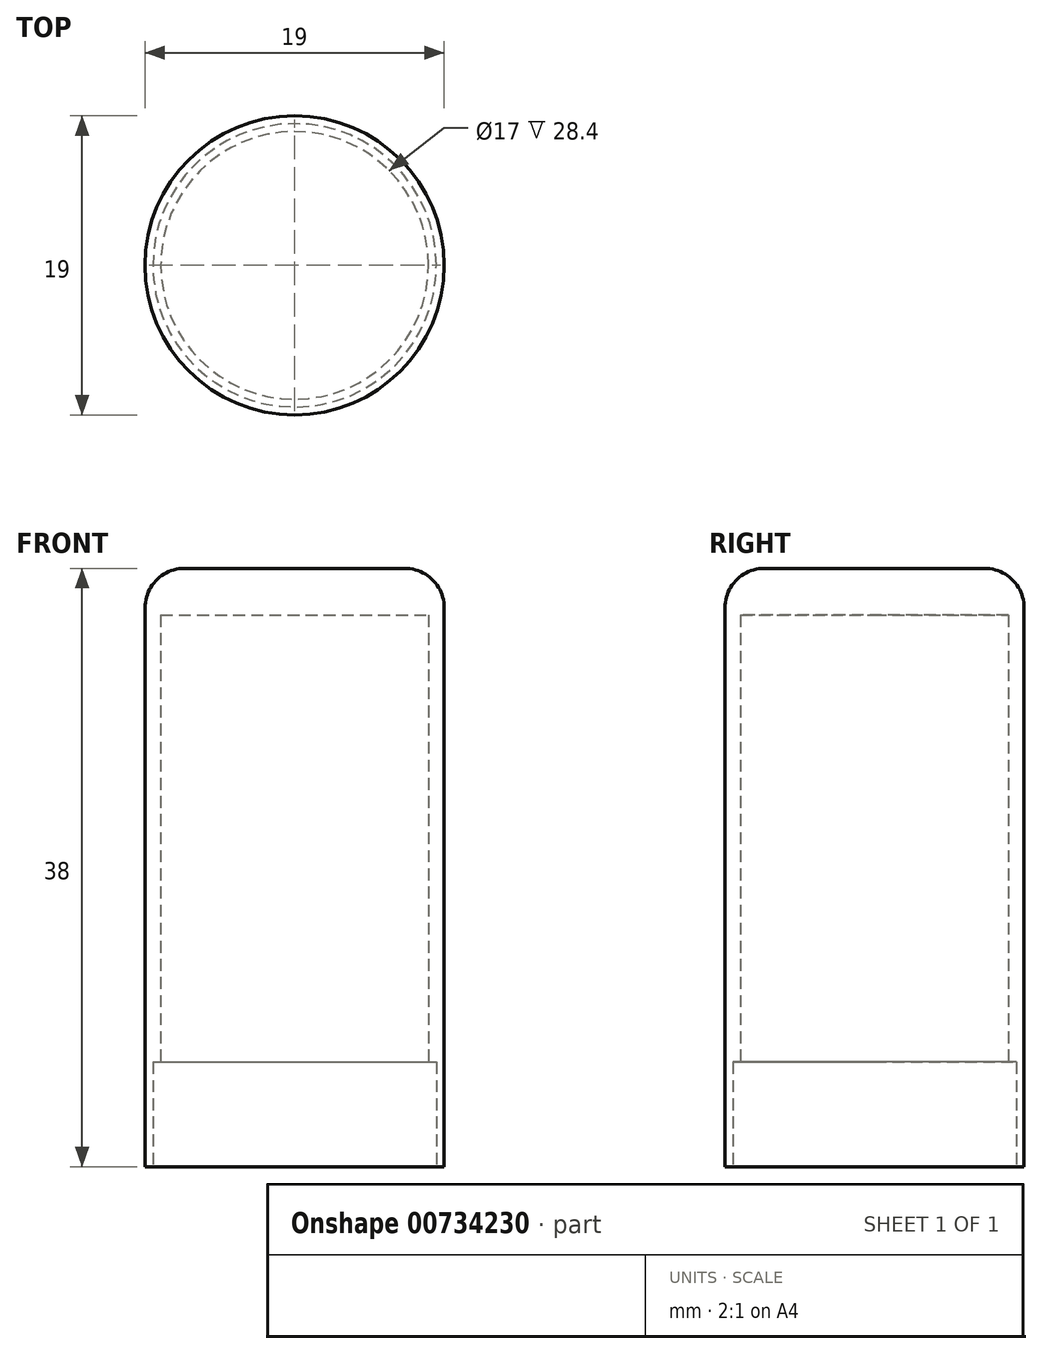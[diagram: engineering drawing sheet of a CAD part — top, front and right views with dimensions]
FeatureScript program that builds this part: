
annotation { "Feature Type Name" : "Feature", "Feature Type Description" : "" }
export const myFeature = defineFeature(function(context is Context, id is Id, definition is map)
    precondition{}
    {
        {
            var Q0;
            Q0=qCreatedBy(makeId("Top.planeOp"),FACE);
            var sketch = newSketch(context, id + "F0", { "sketchPlane" : qUnion([Q0])});
            skCircle(sketch, "E0", {"center": v(0, 0) * mm, "radius": 9.5 * mm});
            skSolve(sketch);
        }
        {
            var Q0;
            Q0=qSketchRegion(id+"F0",true);
            extrude(context, id + "F1", {"entities" : qUnion([Q0]), "depth" : 38 * mm, "offsetDistance" : 25 * mm});
        }
        {
            var Q0;
            Q0=makeQuery(id+"F1.opExtrude","CAP_EDGE",EDGE,{"disambiguationData":[OSD([sQuery(id+"F0.wireOp",EDGE,"E0")])],"isStart":false});
            fillet(context, id + "F2", {"entities" : qUnion([Q0]), "radius" : 2.5 * mm, "tangentPropagation" : true, "allowEdgeOverflow" : false});
        }
        {
            var Q0;
            Q0=makeQuery(id+"F1.opExtrude","CAP_FACE",FACE,{"disambiguationData":[OSD([sQuery(id+"F0.wireOp",EDGE,"E0")])],"isStart":true});
            var sketch = newSketch(context, id + "F3", { "sketchPlane" : qUnion([Q0])});
            skCircle(sketch, "E1", {"center": v(0, 0) * mm, "radius": 9 * mm});
            skSolve(sketch);
        }
        {
            var Q0;
            Q0=qSketchRegion(id+"F3",true);
            extrude(context, id + "F4", {"entities" : qUnion([Q0]), "operationType" : NewBodyOperationType.REMOVE, "oppositeDirection" : true, "depth" : 6.64 * mm, "offsetDistance" : 25 * mm});
        }
        {
            var Q0;
            Q0=makeQuery(id+"F4.boolean.opBoolean","COPY",FACE,{"derivedFrom":makeQuery(id+"F4.opExtrude","CAP_FACE",FACE,{"disambiguationData":[OSD([sQuery(id+"F3.wireOp",EDGE,"E1")])],"isStart":false})});
            var sketch = newSketch(context, id + "F5", { "sketchPlane" : qUnion([Q0])});
            skCircle(sketch, "E2", {"center": v(0, 0) * mm, "radius": 8.5 * mm});
            skSolve(sketch);
        }
        {
            var Q0;
            Q0=qSketchRegion(id+"F5",true);
            extrude(context, id + "F6", {"entities" : qUnion([Q0]), "operationType" : NewBodyOperationType.REMOVE, "oppositeDirection" : true, "depth" : 28.4 * mm, "offsetDistance" : 25 * mm});
        }
    });
